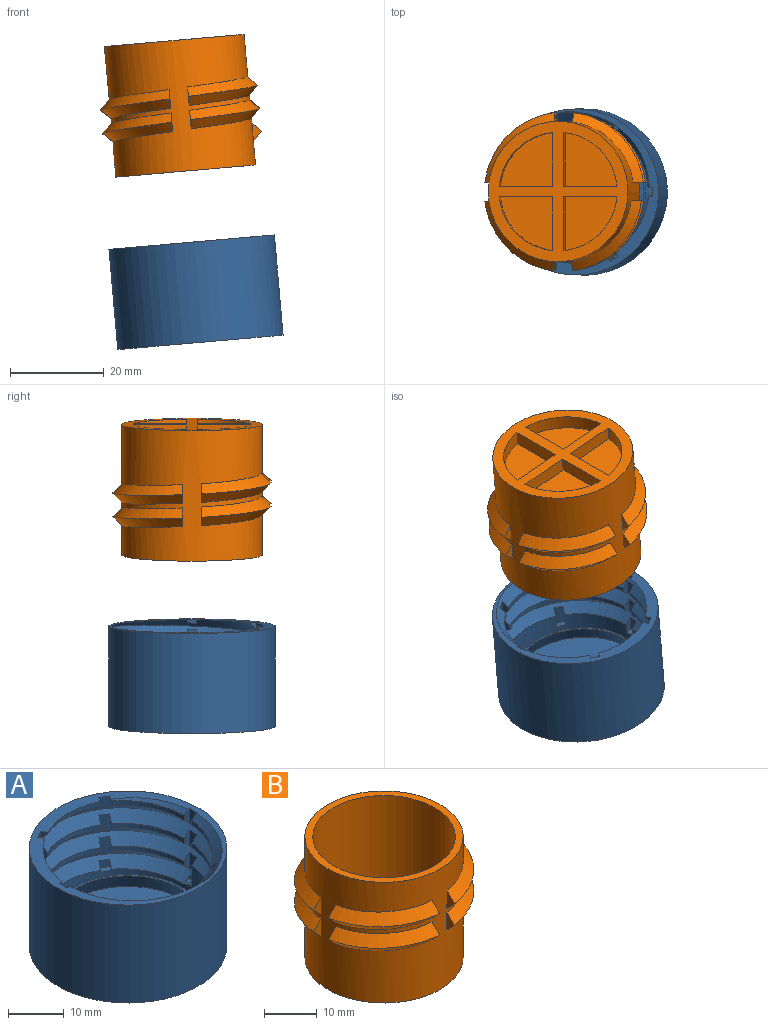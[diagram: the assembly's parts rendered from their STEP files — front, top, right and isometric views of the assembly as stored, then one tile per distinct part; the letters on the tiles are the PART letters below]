
ASSEMBLY  parts=2 mates=1
PART A: 100 faces, bbox 36.3x40.6x25 mm
  f0: cylinder r=15.25mm len=11.68mm, axis (0,0,-1), area 14mm2, adj f18,f21,f37,f79
  f1: cylinder r=15.25mm len=11.68mm, axis (0,0,-1), area 14mm2, adj f18,f21,f35,f76
  f2: cylinder r=15.25mm len=11.68mm, axis (0,0,-1), area 14mm2, adj f17,f21,f32,f73
  f3: cylinder r=15.25mm len=11.68mm, axis (0,0,-1), area 14mm2, adj f18,f21,f61,f68
  f4: cylinder r=15.25mm len=11.68mm, axis (0,0,-1), area 14mm2, adj f18,f21,f58,f65
  f5: cylinder r=15.25mm len=3.9mm, axis (0,0,-1), area 0.8mm2, adj f20,f21,f62
  f6: cylinder r=15.25mm len=13.49mm, axis (0,0,-1), area 14mm2, adj f18,f21,f67,f74
  f7: cylinder r=15.25mm len=13.49mm, axis (0,0,-1), area 14mm2, adj f18,f21,f70,f77
  f8: cylinder r=15.25mm len=13.49mm, axis (0,0,-1), area 14mm2, adj f18,f21,f46,f50
  f9: cylinder r=15.25mm len=13.49mm, axis (0,0,-1), area 14mm2, adj f18,f21,f43,f47
  f10: cylinder r=15.25mm len=11.68mm, axis (0,0,-1), area 14mm2, adj f18,f21,f49,f56
  f11: cylinder r=15.25mm len=11.68mm, axis (0,0,-1), area 14mm2, adj f18,f21,f52,f59
  f12: cylinder r=15.25mm len=11.68mm, axis (0,0,-1), area 14mm2, adj f18,f21,f31,f41
  f13: cylinder r=15.25mm len=13.49mm, axis (0,0,-1), area 10.3mm2, adj f19,f20,f21,f64,f71
  f14: cylinder r=15.25mm len=30.5mm, axis (0,0,-1), area 454.6mm2, adj f16,f18,f29,f38,f39,f80,f82,f83
  f15: cylinder r=15.25mm len=11.68mm, axis (0,0,-1), area 14mm2, adj f18,f21,f34,f44
  f16: plane 0.5x0.5mm, normal (0,1,0), area 0.1mm2, adj f14,f18,f38
  f17: bspline ~14.94x9.63mm, area 11.8mm2, adj f2,f20,f32,f73
  f18: bspline ~39.84x34.5mm, area 787.3mm2, adj f0,f1,f3,f4,f6,f7,f8,f9
  f19: bspline ~17.25x6.71mm, area 0.2mm2, adj f13,f20,f71
  f20: plane 36.29x36.29mm, normal (0,0,1), area 172.4mm2, adj f5,f13,f17,f18,f19,f21,f22,f30
  f21: bspline ~39.84x34.5mm, area 697.8mm2, adj f0,f1,f2,f3,f4,f5,f6,f7
  f22: cylinder r=17.75mm len=35.5mm, axis (0,0,-1), area 2397.8mm2, adj f20,f24
  f23: plane 1.5x0.75mm, normal (0,1,0), area 0.6mm2, adj f18,f21,f36
  f24: plane 35.5x35.5mm, normal (0,0,-1), area 989.8mm2, adj f22
  f25: cone r=14.2mm half-angle=17deg, axis (0,0,-1), area 270.8mm2, adj f27,f28
  f26: cone r=13.68mm half-angle=23.7deg, axis (0,0,-1), area 295.2mm2, adj f27,f29
  f27: plane 27.37x27.37mm, normal (0,0,1), area 33.9mm2, adj f25,f26
  f28: plane 28.4x28.4mm, normal (0,0,1), area 633.5mm2, adj f25
  f29: plane 30.5x30.5mm, normal (0,0,1), area 23.8mm2, adj f14,f26
  f30: plane 3.41x2.09mm, normal (-1,0,0), area 6.5mm2, adj f20,f21,f31,f32
  f31: plane 3.33x1.29mm, normal (0,1,0), area 2.9mm2, adj f12,f18,f20,f21,f30
  f32: plane 3.24x1.29mm, normal (0,-1,0), area 2.9mm2, adj f2,f17,f20,f21,f30
  f33: plane 3.73x2.09mm, normal (-1,0,0), area 7mm2, adj f18,f21,f34,f35
  f34: plane 3.56x1.29mm, normal (0,1,0), area 2.9mm2, adj f15,f18,f21,f33
  f35: plane 3.56x1.29mm, normal (0,-1,0), area 2.9mm2, adj f1,f18,f21,f33
  f36: plane 5.91x2.09mm, normal (-1,0,0), area 10mm2, adj f18,f21,f23,f37,f38,f39,f40
  f37: plane 3.56x1.29mm, normal (0,-1,0), area 2.9mm2, adj f0,f18,f21,f36
  f38: plane 2.01x1.29mm, normal (0,0,1), area 2mm2, adj f14,f16,f18,f36,f39,f40
  f39: plane 5.74x1.29mm, normal (0,1,0), area 6.5mm2, adj f14,f18,f36,f38
  f40: plane 0.83x0.83mm, normal (0,-1,0), area 0.3mm2, adj f18,f36,f38
  f41: plane 3.56x1.11mm, normal (-0.87,-0.5,0), area 2.9mm2, adj f12,f18,f21,f42
  f42: plane 3.73x1.82mm, normal (-0.5,0.87,0), area 7mm2, adj f18,f21,f41,f43
  f43: plane 3.56x1.11mm, normal (0.87,0.5,0), area 2.9mm2, adj f9,f18,f21,f42
  f44: plane 3.56x1.11mm, normal (-0.87,-0.5,0), area 2.9mm2, adj f15,f18,f21,f45
  f45: plane 3.73x1.82mm, normal (-0.5,0.87,0), area 7mm2, adj f18,f21,f44,f46
  f46: plane 3.56x1.11mm, normal (0.87,0.5,0), area 2.9mm2, adj f8,f18,f21,f45
  f47: plane 3.56x1.11mm, normal (-0.87,0.5,0), area 2.9mm2, adj f9,f18,f21,f48
  f48: plane 3.73x1.82mm, normal (0.5,0.87,0), area 7mm2, adj f18,f21,f47,f49
  f49: plane 3.56x1.11mm, normal (0.87,-0.5,0), area 2.9mm2, adj f10,f18,f21,f48
  f50: plane 3.56x1.11mm, normal (-0.87,0.5,0), area 2.9mm2, adj f8,f18,f21,f51
  f51: plane 3.73x1.82mm, normal (0.5,0.87,0), area 7mm2, adj f18,f21,f50,f52
  f52: plane 3.56x1.11mm, normal (0.87,-0.5,0), area 2.9mm2, adj f11,f18,f21,f51
  f53: plane 0.74x0.74mm, normal (0,1,0), area 0.3mm2, adj f20,f21,f54
  f54: plane 2.09x0.91mm, normal (1,0,0), area 1.5mm2, adj f20,f21,f53,f55
  f55: plane 0.83x0.83mm, normal (0,-1,0), area 0.3mm2, adj f20,f21,f54
  f56: plane 3.56x1.29mm, normal (0,1,0), area 2.9mm2, adj f10,f18,f21,f57
  f57: plane 3.73x2.09mm, normal (1,0,0), area 7mm2, adj f18,f21,f56,f58
  f58: plane 3.56x1.29mm, normal (0,-1,0), area 2.9mm2, adj f4,f18,f21,f57
  f59: plane 3.56x1.29mm, normal (0,1,0), area 2.9mm2, adj f11,f18,f21,f60
  f60: plane 3.73x2.09mm, normal (1,0,0), area 7mm2, adj f18,f21,f59,f61
  f61: plane 3.56x1.29mm, normal (0,-1,0), area 2.9mm2, adj f3,f18,f21,f60
  f62: plane 1.57x1.11mm, normal (0.87,0.5,0), area 1.2mm2, adj f5,f20,f21,f63
  f63: plane 1.82x1.74mm, normal (0.5,-0.87,0), area 3.2mm2, adj f20,f21,f62,f64
  f64: plane 1.66x1.11mm, normal (-0.87,-0.5,0), area 1.3mm2, adj f13,f20,f21,f63
  f65: plane 3.56x1.11mm, normal (0.87,0.5,0), area 2.9mm2, adj f4,f18,f21,f66
  f66: plane 3.73x1.82mm, normal (0.5,-0.87,0), area 7mm2, adj f18,f21,f65,f67
  f67: plane 3.56x1.11mm, normal (-0.87,-0.5,0), area 2.9mm2, adj f6,f18,f21,f66
  f68: plane 3.56x1.11mm, normal (0.87,0.5,0), area 2.9mm2, adj f3,f18,f21,f69
  f69: plane 3.73x1.82mm, normal (0.5,-0.87,0), area 7mm2, adj f18,f21,f68,f70
  f70: plane 3.56x1.11mm, normal (-0.87,-0.5,0), area 2.9mm2, adj f7,f18,f21,f69
  f71: plane 2.41x1.11mm, normal (0.87,-0.5,0), area 2.3mm2, adj f13,f19,f20,f21,f72
  f72: plane 2.58x1.82mm, normal (-0.5,-0.87,0), area 4.9mm2, adj f20,f21,f71,f73
  f73: plane 2.49x1.11mm, normal (-0.87,0.5,0), area 2.4mm2, adj f2,f17,f20,f21,f72
  f74: plane 3.56x1.11mm, normal (0.87,-0.5,0), area 2.9mm2, adj f6,f18,f21,f75
  f75: plane 3.73x1.82mm, normal (-0.5,-0.87,0), area 7mm2, adj f18,f21,f74,f76
  f76: plane 3.56x1.11mm, normal (-0.87,0.5,0), area 2.9mm2, adj f1,f18,f21,f75
  f77: plane 3.56x1.11mm, normal (0.87,-0.5,0), area 2.9mm2, adj f7,f18,f21,f78
  f78: plane 3.73x1.82mm, normal (-0.5,-0.87,0), area 7mm2, adj f18,f21,f77,f79
  f79: plane 3.56x1.11mm, normal (-0.87,0.5,0), area 2.9mm2, adj f0,f18,f21,f78
  f80: plane 4.99x1.11mm, normal (-0.87,-0.5,0), area 5.6mm2, adj f14,f18,f81,f83
  f81: plane 5.08x1.82mm, normal (-0.5,0.87,0), area 9.9mm2, adj f18,f80,f82,f83
  f82: plane 4.91x1.11mm, normal (0.87,0.5,0), area 5.5mm2, adj f14,f18,f81,f83
  f83: plane 2.37x2.11mm, normal (0,0,1), area 2.5mm2, adj f14,f80,f81,f82
  f84: plane 4.16x1.11mm, normal (-0.87,0.5,0), area 4.5mm2, adj f14,f18,f85,f87
  f85: plane 4.24x1.82mm, normal (0.5,0.87,0), area 8.2mm2, adj f18,f84,f86,f87
  f86: plane 4.07x1.11mm, normal (0.87,-0.5,0), area 4.4mm2, adj f14,f18,f85,f87
  f87: plane 2.37x2.11mm, normal (0,0,1), area 2.5mm2, adj f14,f84,f85,f86
  f88: plane 3.33x1.29mm, normal (0,1,0), area 3.4mm2, adj f14,f18,f89,f91
  f89: plane 3.41x2.09mm, normal (1,0,0), area 6.5mm2, adj f18,f88,f90,f91
  f90: plane 3.24x1.29mm, normal (0,-1,0), area 3.3mm2, adj f14,f18,f89,f91
  f91: plane 2x1.28mm, normal (0,0,1), area 2.5mm2, adj f14,f88,f89,f90
  f92: plane 2.49x1.11mm, normal (0.87,0.5,0), area 2.4mm2, adj f14,f18,f93,f95
  f93: plane 2.58x1.82mm, normal (0.5,-0.87,0), area 4.9mm2, adj f18,f92,f94,f95
  f94: plane 2.41x1.11mm, normal (-0.87,-0.5,0), area 2.3mm2, adj f14,f18,f93,f95
  f95: plane 2.37x2.11mm, normal (0,0,1), area 2.5mm2, adj f14,f92,f93,f94
  f96: plane 2.37x2.11mm, normal (0,0,1), area 2.5mm2, adj f14,f97,f98,f99
  f97: plane 1.57x1.11mm, normal (-0.87,0.5,0), area 1.2mm2, adj f14,f18,f96,f98
  f98: plane 1.82x1.74mm, normal (-0.5,-0.87,0), area 3.2mm2, adj f18,f96,f97,f99
  f99: plane 1.66x1.11mm, normal (0.87,-0.5,0), area 1.3mm2, adj f14,f18,f96,f98
PART B: 53 faces, bbox 34x39.3x28 mm
  f0: bspline ~25.5x19.63mm, area 59.7mm2, adj f7,f15,f40,f52
  f1: bspline ~25.5x19.63mm, area 59.7mm2, adj f8,f15,f38,f49
  f2: bspline ~25.5x19.63mm, area 59.7mm2, adj f9,f15,f44,f47
  f3: bspline ~25.5x19.63mm, area 59.7mm2, adj f10,f15,f42,f46
  f4: bspline ~25.5x19.63mm, area 59.7mm2, adj f11,f15,f39,f43
  f5: bspline ~25.5x19.63mm, area 59.7mm2, adj f12,f15,f37,f41
  f6: bspline ~25.5x19.63mm, area 59.7mm2, adj f13,f15,f45,f50
  f7: bspline ~25.5x19.63mm, area 59.7mm2, adj f0,f15,f40,f52
  f8: bspline ~25.5x19.63mm, area 59.7mm2, adj f1,f15,f38,f49
  f9: bspline ~25.5x19.63mm, area 59.7mm2, adj f2,f15,f44,f47
  f10: bspline ~25.5x19.63mm, area 59.7mm2, adj f3,f15,f42,f46
  f11: bspline ~25.5x19.63mm, area 59.7mm2, adj f4,f15,f39,f43
  f12: bspline ~25.5x19.63mm, area 59.7mm2, adj f5,f15,f37,f41
  f13: bspline ~25.5x19.63mm, area 59.7mm2, adj f6,f15,f45,f50
  f14: cylinder r=13.5mm len=27mm, axis (0,0,-1), area 1950.9mm2, adj f16,f19
  f15: cylinder r=15mm len=30mm, axis (0,0,-1), area 2013.3mm2, adj f0,f1,f2,f3,f4,f5,f6,f7
  f16: plane 30x30mm, normal (0,0,1), area 134.3mm2, adj f14,f15
  f17: bspline ~25.5x19.63mm, area 59.7mm2, adj f15,f18,f48,f51
  f18: bspline ~25.5x19.63mm, area 59.7mm2, adj f15,f17,f48,f51
  f19: plane 27x27mm, normal (0,0,1), area 572.6mm2, adj f14
  f20: cylinder r=12.66mm len=11.49mm, axis (0,0,1), area 52.6mm2, adj f21,f31,f32,f33
  f21: plane 11.37x3mm, normal (0,-1,0), area 34.1mm2, adj f20,f31,f32,f33
  f22: plane 11.37x3mm, normal (0,1,0), area 34.1mm2, adj f23,f28,f32,f34
  f23: plane 11.49x3mm, normal (-1,0,0), area 34.5mm2, adj f22,f28,f32,f34
  f24: plane 11.37x3mm, normal (0,1,0), area 34.1mm2, adj f25,f29,f32,f35
  f25: cylinder r=12.66mm len=11.49mm, axis (0,0,1), area 52.6mm2, adj f24,f29,f32,f35
  f26: cylinder r=12.66mm len=11.49mm, axis (0,0,1), area 52.6mm2, adj f27,f30,f32,f36
  f27: plane 11.49x3mm, normal (-1,0,0), area 34.5mm2, adj f26,f30,f32,f36
  f28: cylinder r=12.66mm len=11.49mm, axis (0,0,1), area 52.6mm2, adj f22,f23,f32,f34
  f29: plane 11.49x3mm, normal (1,0,0), area 34.5mm2, adj f24,f25,f32,f35
  f30: plane 11.37x3mm, normal (0,-1,0), area 34.1mm2, adj f26,f27,f32,f36
  f31: plane 11.49x3mm, normal (1,0,0), area 34.5mm2, adj f20,f21,f32,f33
  f32: plane 30x30mm, normal (0,0,-1), area 316.6mm2, adj f15,f20,f21,f22,f23,f24,f25,f26
  f33: plane 11.49x11.37mm, normal (0,0,-1), area 97.6mm2, adj f20,f21,f31
  f34: plane 11.49x11.37mm, normal (0,0,-1), area 97.6mm2, adj f22,f23,f28
  f35: plane 11.49x11.37mm, normal (0,0,-1), area 97.6mm2, adj f24,f25,f29
  f36: plane 11.49x11.37mm, normal (0,0,-1), area 97.6mm2, adj f26,f27,f30
  f37: plane 4.02x2.03mm, normal (-1,0,0), area 4mm2, adj f5,f12,f15
  f38: plane 4.02x2.03mm, normal (1,0,0), area 4mm2, adj f1,f8,f15
  f39: plane 4.02x2.03mm, normal (-1,0,0), area 4mm2, adj f4,f11,f15
  f40: plane 4.02x2.03mm, normal (1,0,0), area 4mm2, adj f0,f7,f15
  f41: plane 4.02x2.03mm, normal (0,1,0), area 4mm2, adj f5,f12,f15
  f42: plane 4.02x2.03mm, normal (0,-1,0), area 4mm2, adj f3,f10,f15
  f43: plane 4.02x2.03mm, normal (0,1,0), area 4mm2, adj f4,f11,f15
  f44: plane 4.02x2.03mm, normal (0,-1,0), area 4mm2, adj f2,f9,f15
  f45: plane 4.02x2.03mm, normal (1,0,0), area 4mm2, adj f6,f13,f15
  f46: plane 4.02x2.03mm, normal (-1,0,0), area 4mm2, adj f3,f10,f15
  f47: plane 4.02x2.03mm, normal (-1,0,0), area 4mm2, adj f2,f9,f15
  f48: plane 4.02x2.03mm, normal (1,0,0), area 4mm2, adj f15,f17,f18
  f49: plane 4.02x2.03mm, normal (0,1,0), area 4mm2, adj f1,f8,f15
  f50: plane 4.02x2.03mm, normal (0,-1,0), area 4mm2, adj f6,f13,f15
  f51: plane 4.02x2.03mm, normal (0,-1,0), area 4mm2, adj f15,f17,f18
  f52: plane 4.02x2.03mm, normal (0,1,0), area 4mm2, adj f0,f7,f15
PLACE A rot(axis=(0.04,0,-1),180deg) t=(-1.95,-0.72,40.34)mm
PLACE B rot(axis=(-1,0,-0.04),180deg) t=(-6.64,-0.72,93.88)mm
MATE revolute B.f15 <-> A.f22  axis (-0.09,0,1) through (-6.12,-0.72,87.9)mm
